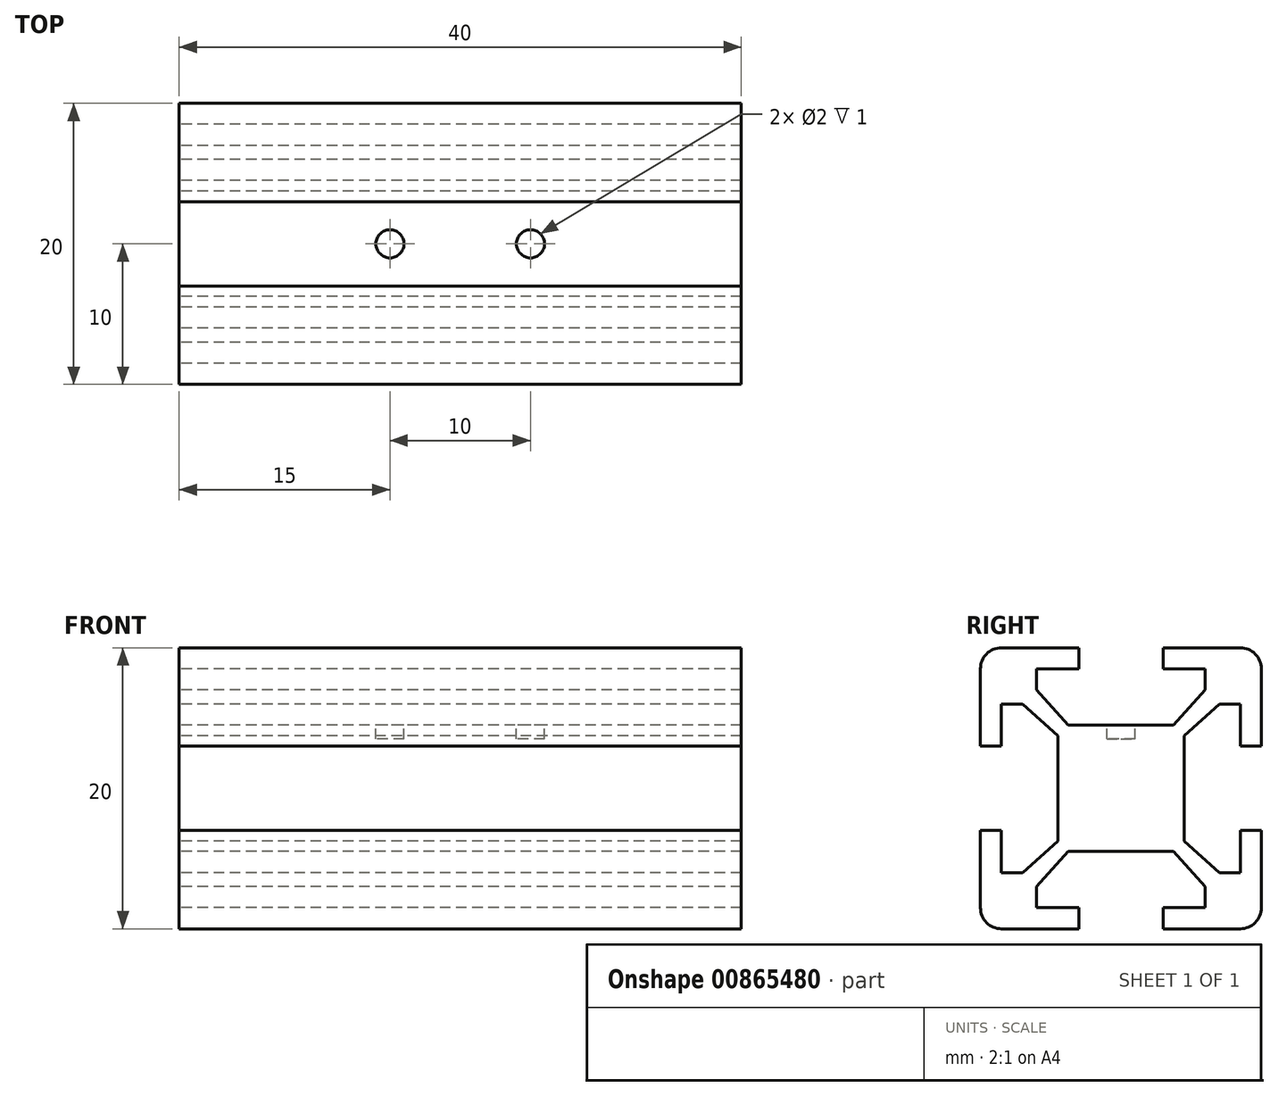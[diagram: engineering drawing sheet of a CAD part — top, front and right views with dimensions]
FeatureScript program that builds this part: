
annotation { "Feature Type Name" : "Feature", "Feature Type Description" : "" }
export const myFeature = defineFeature(function(context is Context, id is Id, definition is map)
    precondition{}
    {
        {
            var Q0;
            Q0=qCreatedBy(makeId("Right.planeOp"),FACE);
            var sketch = newSketch(context, id + "F0", { "sketchPlane" : qUnion([Q0])});
            skLineSegment(sketch, "E0.bottom", {"start": v(8.5, 10) * mm, "end": v(3, 10) * mm});
            skLineSegment(sketch, "E0.top", {"start": v(8.5, -10) * mm, "end": v(-8.5, -10) * mm});
            skLineSegment(sketch, "E0.left", {"start": v(10, 8.5) * mm, "end": v(10, 3) * mm});
            skLineSegment(sketch, "E0.right", {"start": v(-10, 8.5) * mm, "end": v(-10, 3) * mm});
            skPoint(sketch, "E0.middle", {"position": v(0, 0) * mm});
            skPoint(sketch, "E1.visualSharp", {"position": v(-10, 10) * mm});
            skArc(sketch, "E1.filletArc", {"start": v(-8.5, 10) * mm, "mid": v(-9.56, 9.56) * mm, "end": v(-10, 8.5) * mm});
            skPoint(sketch, "E2.visualSharp", {"position": v(10, 10) * mm});
            skArc(sketch, "E2.filletArc", {"start": v(10, 8.5) * mm, "mid": v(9.56, 9.56) * mm, "end": v(8.5, 10) * mm});
            skPoint(sketch, "E3.visualSharp", {"position": v(10, -10) * mm});
            skArc(sketch, "E3.filletArc", {"start": v(8.5, -10) * mm, "mid": v(9.56, -9.56) * mm, "end": v(10, -8.5) * mm});
            skPoint(sketch, "E4.visualSharp", {"position": v(-10, -10) * mm});
            skArc(sketch, "E4.filletArc", {"start": v(-10, -8.5) * mm, "mid": v(-9.56, -9.56) * mm, "end": v(-8.5, -10) * mm});
            skLineSegment(sketch, "E5", {"start": v(-3, 10) * mm, "end": v(-3, 8.5) * mm});
            skLineSegment(sketch, "E6", {"start": v(-3, 8.5) * mm, "end": v(-6, 8.5) * mm});
            skLineSegment(sketch, "E7", {"start": v(-6, 8.5) * mm, "end": v(-6, 7) * mm});
            skLineSegment(sketch, "E8", {"start": v(-6, 7) * mm, "end": v(-3.75, 4.5) * mm});
            skLineSegment(sketch, "E9", {"start": v(-3.75, 4.5) * mm, "end": v(0, 4.5) * mm});
            skLineSegment(sketch, "E10.MirrorCS", {"start": v(3, 10) * mm, "end": v(3, 8.5) * mm});
            skLineSegment(sketch, "E11.MirrorCS", {"start": v(3, 8.5) * mm, "end": v(6, 8.5) * mm});
            skLineSegment(sketch, "E12.MirrorCS", {"start": v(6, 8.5) * mm, "end": v(6, 7) * mm});
            skLineSegment(sketch, "E13.MirrorCS", {"start": v(6, 7) * mm, "end": v(3.75, 4.5) * mm});
            skLineSegment(sketch, "E14.MirrorCS", {"start": v(3.75, 4.5) * mm, "end": v(0, 4.5) * mm});
            skLineSegment(sketch, "E15.trimOffspring", {"start": v(-3, 10) * mm, "end": v(-8.5, 10) * mm});
            skLineSegment(sketch, "E16.1.0", {"start": v(-8.5, -3) * mm, "end": v(-8.5, -6) * mm});
            skLineSegment(sketch, "E16.1.1", {"start": v(-8.5, -6) * mm, "end": v(-7, -6) * mm});
            skLineSegment(sketch, "E16.1.2", {"start": v(-7, -6) * mm, "end": v(-4.5, -3.75) * mm});
            skLineSegment(sketch, "E16.1.3", {"start": v(-4.5, -3.75) * mm, "end": v(-4.5, 0) * mm});
            skLineSegment(sketch, "E16.1.4", {"start": v(-4.5, 3.75) * mm, "end": v(-4.5, 0) * mm});
            skLineSegment(sketch, "E16.1.5", {"start": v(-7, 6) * mm, "end": v(-4.5, 3.75) * mm});
            skLineSegment(sketch, "E16.1.6", {"start": v(-8.5, 6) * mm, "end": v(-7, 6) * mm});
            skLineSegment(sketch, "E16.1.7", {"start": v(-8.5, 3) * mm, "end": v(-8.5, 6) * mm});
            skLineSegment(sketch, "E16.1.8", {"start": v(-10, 3) * mm, "end": v(-8.5, 3) * mm});
            skLineSegment(sketch, "E16.1.9", {"start": v(-10, -3) * mm, "end": v(-8.5, -3) * mm});
            skLineSegment(sketch, "E16.2.0", {"start": v(3, -8.5) * mm, "end": v(6, -8.5) * mm});
            skLineSegment(sketch, "E16.2.1", {"start": v(6, -8.5) * mm, "end": v(6, -7) * mm});
            skLineSegment(sketch, "E16.2.2", {"start": v(6, -7) * mm, "end": v(3.75, -4.5) * mm});
            skLineSegment(sketch, "E16.2.3", {"start": v(3.75, -4.5) * mm, "end": v(0, -4.5) * mm});
            skLineSegment(sketch, "E16.2.4", {"start": v(-3.75, -4.5) * mm, "end": v(0, -4.5) * mm});
            skLineSegment(sketch, "E16.2.5", {"start": v(-6, -7) * mm, "end": v(-3.75, -4.5) * mm});
            skLineSegment(sketch, "E16.2.6", {"start": v(-6, -8.5) * mm, "end": v(-6, -7) * mm});
            skLineSegment(sketch, "E16.2.7", {"start": v(-3, -8.5) * mm, "end": v(-6, -8.5) * mm});
            skLineSegment(sketch, "E16.2.8", {"start": v(-3, -10) * mm, "end": v(-3, -8.5) * mm});
            skLineSegment(sketch, "E16.2.9", {"start": v(3, -10) * mm, "end": v(3, -8.5) * mm});
            skLineSegment(sketch, "E16.3.0", {"start": v(8.5, 3) * mm, "end": v(8.5, 6) * mm});
            skLineSegment(sketch, "E16.3.1", {"start": v(8.5, 6) * mm, "end": v(7, 6) * mm});
            skLineSegment(sketch, "E16.3.2", {"start": v(7, 6) * mm, "end": v(4.5, 3.75) * mm});
            skLineSegment(sketch, "E16.3.3", {"start": v(4.5, 3.75) * mm, "end": v(4.5, 0) * mm});
            skLineSegment(sketch, "E16.3.4", {"start": v(4.5, -3.75) * mm, "end": v(4.5, 0) * mm});
            skLineSegment(sketch, "E16.3.5", {"start": v(7, -6) * mm, "end": v(4.5, -3.75) * mm});
            skLineSegment(sketch, "E16.3.6", {"start": v(8.5, -6) * mm, "end": v(7, -6) * mm});
            skLineSegment(sketch, "E16.3.7", {"start": v(8.5, -3) * mm, "end": v(8.5, -6) * mm});
            skLineSegment(sketch, "E16.3.8", {"start": v(10, -3) * mm, "end": v(8.5, -3) * mm});
            skLineSegment(sketch, "E16.3.9", {"start": v(10, 3) * mm, "end": v(8.5, 3) * mm});
            skLineSegment(sketch, "E17.trimOffspring", {"start": v(-10, -3) * mm, "end": v(-10, -8.5) * mm});
            skLineSegment(sketch, "E18.trimOffspring", {"start": v(10, -3) * mm, "end": v(10, -8.5) * mm});
            skSolve(sketch);
        }
        {
            var Q0;
            Q0=makeQuery(id+"F0.imprint","IMPRINT",FACE,{"disambiguationData":[TD([[makeQuery(id+"F0.imprint","IMPRINT",EDGE,{"derivedFrom":sQuery(id+"F0.wireOp",EDGE,"E0.bottom")}),1.0]])]});
            extrude(context, id + "F1", {"entities" : qUnion([Q0]), "depth" : 40 * mm, "offsetDistance" : 25 * mm});
        }
        {
            var Q0;
            Q0=makeQuery(id+"F1.opExtrude","SWEPT_FACE",FACE,{"disambiguationData":[OSD([sQuery(id+"F0.wireOp",EDGE,"E9"),sQuery(id+"F0.wireOp",EDGE,"E14.MirrorCS")])]});
            var sketch = newSketch(context, id + "F2", { "sketchPlane" : qUnion([Q0])});
            skCircle(sketch, "E19", {"center": v(15, 0) * mm, "radius": 1 * mm});
            skCircle(sketch, "E20", {"center": v(25, 0) * mm, "radius": 1 * mm});
            skSolve(sketch);
        }
        {
            var Q0;
            Q0=qSketchRegion(id+"F2",true);
            extrude(context, id + "F3", {"entities" : qUnion([Q0]), "operationType" : NewBodyOperationType.REMOVE, "oppositeDirection" : true, "depth" : 1 * mm, "offsetDistance" : 25 * mm});
        }
    });
